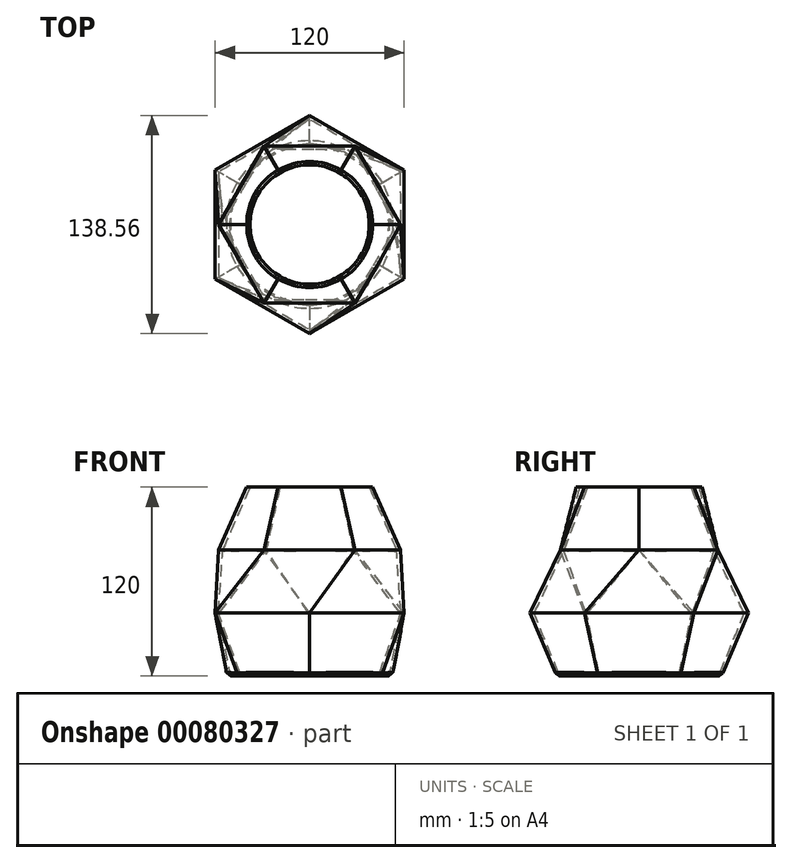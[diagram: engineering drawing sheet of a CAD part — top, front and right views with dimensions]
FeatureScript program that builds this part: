
annotation { "Feature Type Name" : "Feature", "Feature Type Description" : "" }
export const myFeature = defineFeature(function(context is Context, id is Id, definition is map)
    precondition{}
    {
        {
            var Q0;
            Q0=qCreatedBy(makeId("Top.planeOp"),FACE);
            cPlane(context, id + "F0", {"entities" : qUnion([Q0]), "cplaneType" : CPlaneType.OFFSET, "offset" : 40 * mm, "width" : 150 * mm, "height" : 150 * mm});
        }
        {
            var Q0;
            Q0=qCreatedBy(id+"F0.planeOp",FACE);
            cPlane(context, id + "F1", {"entities" : qUnion([Q0]), "cplaneType" : CPlaneType.OFFSET, "offset" : 40 * mm, "width" : 150 * mm, "height" : 150 * mm});
        }
        {
            var Q0;
            Q0=qCreatedBy(id+"F1.planeOp",FACE);
            cPlane(context, id + "F2", {"entities" : qUnion([Q0]), "cplaneType" : CPlaneType.OFFSET, "offset" : 40 * mm, "width" : 150 * mm, "height" : 150 * mm});
        }
        {
            var Q0;
            Q0=qCreatedBy(makeId("Top.planeOp"),FACE);
            var sketch = newSketch(context, id + "F3", { "sketchPlane" : qUnion([Q0])});
            skCircle(sketch, "E0", {"center": v(0, 0) * mm, "radius": 52.5 * mm});
            skSolve(sketch);
        }
        {
            var Q0;
            Q0=qCreatedBy(id+"F0.planeOp",FACE);
            var sketch = newSketch(context, id + "F4", { "sketchPlane" : qUnion([Q0])});
            skCircle(sketch, "E1.cCircle", {"center": v(0, 0) * mm, "radius": 60 * mm, "construction": true});
            skLineSegment(sketch, "E1.0", {"start": v(0, 69.28) * mm, "end": v(60, 34.64) * mm});
            skLineSegment(sketch, "E1.1", {"start": v(60, 34.64) * mm, "end": v(60, -34.64) * mm});
            skLineSegment(sketch, "E1.2", {"start": v(60, -34.64) * mm, "end": v(0, -69.28) * mm});
            skLineSegment(sketch, "E1.3", {"start": v(0, -69.28) * mm, "end": v(-60, -34.64) * mm});
            skLineSegment(sketch, "E1.4", {"start": v(-60, -34.64) * mm, "end": v(-60, 34.64) * mm});
            skLineSegment(sketch, "E1.5", {"start": v(-60, 34.64) * mm, "end": v(0, 69.28) * mm});
            skPoint(sketch, "E1.0.midPoint", {"position": v(30, 51.96) * mm});
            skSolve(sketch);
        }
        {
            var Q0;
            Q0=makeQuery(id+"F3.imprint","IMPRINT",FACE,{"disambiguationData":[TD([[makeQuery(id+"F3.imprint","IMPRINT",EDGE,{"derivedFrom":sQuery(id+"F3.wireOp",EDGE,"E0")}),1.0]])]});
            var Q1;
            Q1=makeQuery(id+"F4.imprint","IMPRINT",FACE,{"disambiguationData":[TD([[makeQuery(id+"F4.imprint","IMPRINT",EDGE,{"derivedFrom":sQuery(id+"F4.wireOp",EDGE,"E1.0")}),-1.0]])]});
            loft(context, id + "F5", {"sheetProfilesArray" : [{ "sheetProfileEntities" : qUnion([Q0]) }, { "sheetProfileEntities" : qUnion([Q1]) }]});
        }
        {
            var Q0;
            Q0=qCreatedBy(id+"F1.planeOp",FACE);
            var sketch = newSketch(context, id + "F6", { "sketchPlane" : qUnion([Q0])});
            skCircle(sketch, "E2.cCircle", {"center": v(0, 0) * mm, "radius": 50 * mm, "construction": true});
            skLineSegment(sketch, "E2.0", {"start": v(28.87, 50) * mm, "end": v(57.74, 0) * mm});
            skLineSegment(sketch, "E2.1", {"start": v(57.74, 0) * mm, "end": v(28.87, -50) * mm});
            skLineSegment(sketch, "E2.2", {"start": v(28.87, -50) * mm, "end": v(-28.87, -50) * mm});
            skLineSegment(sketch, "E2.3", {"start": v(-28.87, -50) * mm, "end": v(-57.74, 0) * mm});
            skLineSegment(sketch, "E2.4", {"start": v(-57.74, 0) * mm, "end": v(-28.87, 50) * mm});
            skLineSegment(sketch, "E2.5", {"start": v(-28.87, 50) * mm, "end": v(28.87, 50) * mm});
            skPoint(sketch, "E2.0.midPoint", {"position": v(43.3, 25) * mm});
            skSolve(sketch);
        }
        {
            var Q1;
            Q1=makeQuery(id+"F5.opLoft","CAP_FACE",FACE,{"disambiguationData":[OSD([makeQuery(id+"F4.imprint","IMPRINT",FACE,{"disambiguationData":[TD([[makeQuery(id+"F4.imprint","IMPRINT",EDGE,{"derivedFrom":sQuery(id+"F4.wireOp",EDGE,"E1.0")}),-1.0]])]})])],"isStart":true});
            var Q2;
            Q2=makeQuery(id+"F6.imprint","IMPRINT",FACE,{"disambiguationData":[TD([[makeQuery(id+"F6.imprint","IMPRINT",EDGE,{"derivedFrom":sQuery(id+"F6.wireOp",EDGE,"E2.0")}),-1.0]])]});
            loft(context, id + "F7", {"operationType" : NewBodyOperationType.ADD, "sheetProfilesArray" : [{ "sheetProfileEntities" : qUnion([Q1]) }, { "sheetProfileEntities" : qUnion([Q2]) }]});
        }
        {
            var Q0;
            Q0=qCreatedBy(id+"F2.planeOp",FACE);
            var sketch = newSketch(context, id + "F8", { "sketchPlane" : qUnion([Q0])});
            skCircle(sketch, "E3", {"center": v(0, 0) * mm, "radius": 40 * mm});
            skSolve(sketch);
        }
        {
            var Q1;
            Q1=makeQuery(id+"F7.opLoft","CAP_FACE",FACE,{"disambiguationData":[OSD([makeQuery(id+"F6.imprint","IMPRINT",FACE,{"disambiguationData":[TD([[makeQuery(id+"F6.imprint","IMPRINT",EDGE,{"derivedFrom":sQuery(id+"F6.wireOp",EDGE,"E2.0")}),-1.0]])]})])],"isStart":true});
            var Q2;
            Q2=makeQuery(id+"F8.imprint","IMPRINT",FACE,{"disambiguationData":[TD([[makeQuery(id+"F8.imprint","IMPRINT",EDGE,{"derivedFrom":sQuery(id+"F8.wireOp",EDGE,"E3")}),1.0]])]});
            loft(context, id + "F9", {"operationType" : NewBodyOperationType.ADD, "sheetProfilesArray" : [{ "sheetProfileEntities" : qUnion([Q1]) }, { "sheetProfileEntities" : qUnion([Q2]) }]});
        }
        {
            var Q0;
            Q0=makeQuery(id+"F9.opLoft","CAP_FACE",FACE,{"disambiguationData":[OSD([makeQuery(id+"F8.imprint","IMPRINT",FACE,{"disambiguationData":[TD([[makeQuery(id+"F8.imprint","IMPRINT",EDGE,{"derivedFrom":sQuery(id+"F8.wireOp",EDGE,"E3")}),1.0]])]})])],"isStart":true});
            shell(context, id + "F10", {"entities" : qUnion([Q0]), "thickness" : 2 * mm});
        }
        {
            var Q0;
            Q0=makeQuery(id+"F5.opLoft","CAP_FACE",FACE,{"disambiguationData":[OSD([makeQuery(id+"F3.imprint","IMPRINT",FACE,{"disambiguationData":[TD([[makeQuery(id+"F3.imprint","IMPRINT",EDGE,{"derivedFrom":sQuery(id+"F3.wireOp",EDGE,"E0")}),1.0]])]})])],"isStart":true});
            chamfer(context, id + "F11", {"entities" : qUnion([Q0]), "width" : 3 * mm, "tangentPropagation" : true});
        }
    });
